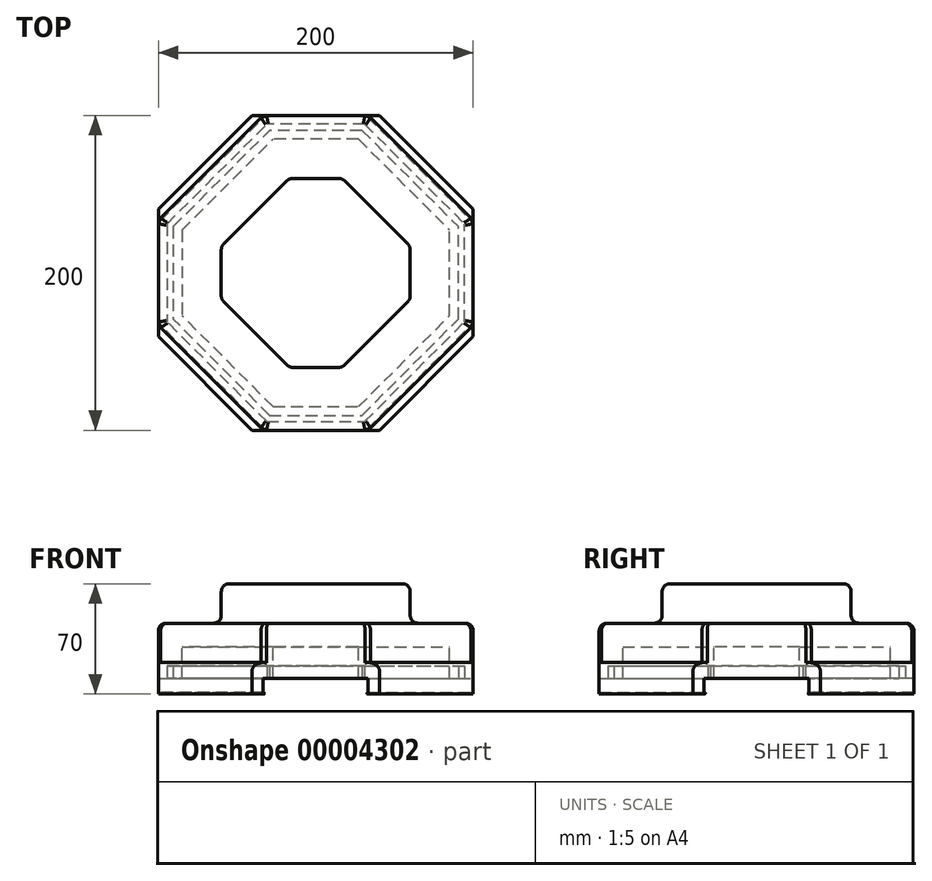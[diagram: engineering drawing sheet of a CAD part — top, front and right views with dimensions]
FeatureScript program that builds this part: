
annotation { "Feature Type Name" : "Feature", "Feature Type Description" : "" }
export const myFeature = defineFeature(function(context is Context, id is Id, definition is map)
    precondition{}
    {
        {
            var Q0;
            Q0=qCreatedBy(makeId("Top.planeOp"),FACE);
            var sketch = newSketch(context, id + "F0", { "sketchPlane" : qUnion([Q0])});
            skLineSegment(sketch, "E0", {"start": v(-113, -132.84) * mm, "end": v(87, -132.84) * mm});
            skLineSegment(sketch, "E1", {"start": v(87, -132.84) * mm, "end": v(87, 67.16) * mm});
            skLineSegment(sketch, "E2", {"start": v(87, 67.16) * mm, "end": v(-113, 67.16) * mm});
            skLineSegment(sketch, "E3", {"start": v(-113, 67.16) * mm, "end": v(-113, -132.84) * mm});
            skLineSegment(sketch, "E4.0", {"start": v(-113, -66.17) * mm, "end": v(87, -66.17) * mm});
            skLineSegment(sketch, "E5.0", {"start": v(-113, 0.5) * mm, "end": v(87, 0.5) * mm});
            skLineSegment(sketch, "E6.0", {"start": v(-46.33, 67.16) * mm, "end": v(-46.33, -132.84) * mm});
            skLineSegment(sketch, "E7.0", {"start": v(20.33, -132.84) * mm, "end": v(20.33, 67.16) * mm});
            skLineSegment(sketch, "E8", {"start": v(-46.33, -132.84) * mm, "end": v(-113, -66.17) * mm});
            skLineSegment(sketch, "E9", {"start": v(-113, 0.5) * mm, "end": v(-46.33, 67.16) * mm});
            skLineSegment(sketch, "E10", {"start": v(20.33, 67.16) * mm, "end": v(87, 0.5) * mm});
            skLineSegment(sketch, "E11", {"start": v(20.33, -132.84) * mm, "end": v(87, -66.17) * mm});
            skSolve(sketch);
        }
        {
            var Q0;
            {var subQ0=sQuery(id+"F0.wireOp",EDGE,"E8");Q0=makeQuery(id+"F0.imprint","IMPRINT",FACE,{"disambiguationData":[TD([[makeQuery(id+"F0.imprint","IMPRINT",EDGE,{"derivedFrom":subQ0}),-1.0]])]});}
            var Q1;
            {var subQ1=sQuery(id+"F0.wireOp",EDGE,"E4.0");var subQ5=sQuery(id+"F0.wireOp",EDGE,"E6.0");var subQ6=makeQuery(id+"F0.imprint","INTERSECT",VERTEX,{"derivedFrom":[subQ1,subQ5]});Q1=makeQuery(id+"F0.imprint","IMPRINT",FACE,{"disambiguationData":[TD([[makeQuery(id+"F0.imprint","IMPRINT",EDGE,{"disambiguationData":[TD([[subQ6,-1.0]])],"derivedFrom":subQ1}),-1.0]])]});}
            var Q2;
            {var subQ0=sQuery(id+"F0.wireOp",EDGE,"E11");Q2=makeQuery(id+"F0.imprint","IMPRINT",FACE,{"disambiguationData":[TD([[makeQuery(id+"F0.imprint","IMPRINT",EDGE,{"derivedFrom":subQ0}),1.0]])]});}
            var Q3;
            {var subQ0=sQuery(id+"F0.wireOp",EDGE,"E6.0");var subQ3=sQuery(id+"F0.wireOp",EDGE,"E4.0");var subQ4=makeQuery(id+"F0.imprint","INTERSECT",VERTEX,{"derivedFrom":[subQ3,subQ0]});Q3=makeQuery(id+"F0.imprint","IMPRINT",FACE,{"disambiguationData":[TD([[makeQuery(id+"F0.imprint","IMPRINT",EDGE,{"disambiguationData":[TD([[subQ4,1.0]])],"derivedFrom":subQ0}),-1.0]])]});}
            var Q4;
            {var subQ3=sQuery(id+"F0.wireOp",EDGE,"E4.0");var subQ5=sQuery(id+"F0.wireOp",EDGE,"E6.0");var subQ7=makeQuery(id+"F0.imprint","INTERSECT",VERTEX,{"derivedFrom":[subQ3,subQ5]});Q4=makeQuery(id+"F0.imprint","IMPRINT",FACE,{"disambiguationData":[TD([[makeQuery(id+"F0.imprint","IMPRINT",EDGE,{"disambiguationData":[TD([[subQ7,-1.0]])],"derivedFrom":subQ3}),1.0]])]});}
            var Q5;
            {var subQ0=sQuery(id+"F0.wireOp",EDGE,"E7.0");var subQ3=sQuery(id+"F0.wireOp",EDGE,"E4.0");var subQ4=makeQuery(id+"F0.imprint","INTERSECT",VERTEX,{"derivedFrom":[subQ3,subQ0]});Q5=makeQuery(id+"F0.imprint","IMPRINT",FACE,{"disambiguationData":[TD([[makeQuery(id+"F0.imprint","IMPRINT",EDGE,{"disambiguationData":[TD([[subQ4,-1.0]])],"derivedFrom":subQ0}),-1.0]])]});}
            var Q6;
            {var subQ0=sQuery(id+"F0.wireOp",EDGE,"E10");Q6=makeQuery(id+"F0.imprint","IMPRINT",FACE,{"disambiguationData":[TD([[makeQuery(id+"F0.imprint","IMPRINT",EDGE,{"derivedFrom":subQ0}),-1.0]])]});}
            var Q7;
            {var subQ1=sQuery(id+"F0.wireOp",EDGE,"E5.0");var subQ5=sQuery(id+"F0.wireOp",EDGE,"E6.0");var subQ6=makeQuery(id+"F0.imprint","INTERSECT",VERTEX,{"derivedFrom":[subQ1,subQ5]});Q7=makeQuery(id+"F0.imprint","IMPRINT",FACE,{"disambiguationData":[TD([[makeQuery(id+"F0.imprint","IMPRINT",EDGE,{"disambiguationData":[TD([[subQ6,-1.0]])],"derivedFrom":subQ1}),1.0]])]});}
            var Q8;
            {var subQ0=sQuery(id+"F0.wireOp",EDGE,"E9");Q8=makeQuery(id+"F0.imprint","IMPRINT",FACE,{"disambiguationData":[TD([[makeQuery(id+"F0.imprint","IMPRINT",EDGE,{"derivedFrom":subQ0}),-1.0]])]});}
            extrude(context, id + "F1", {"entities" : qUnion([Q0, Q1, Q2, Q3, Q4, Q5, Q6, Q7, Q8]), "oppositeDirection" : true, "depth" : 15 * mm});
        }
        {
            var Q0;
            Q0=makeQuery(id+"F1.opExtrude","CAP_FACE",FACE,{"disambiguationData":[OSD([sQuery(id+"F0.wireOp",EDGE,"E0"),sQuery(id+"F0.wireOp",EDGE,"E1"),sQuery(id+"F0.wireOp",EDGE,"E2"),sQuery(id+"F0.wireOp",EDGE,"E3"),sQuery(id+"F0.wireOp",EDGE,"E8"),sQuery(id+"F0.wireOp",EDGE,"E9"),sQuery(id+"F0.wireOp",EDGE,"E10"),sQuery(id+"F0.wireOp",EDGE,"E11")])],"isStart":true});
            var sketch = newSketch(context, id + "F2", { "sketchPlane" : qUnion([Q0])});
            skLineSegment(sketch, "E12.0", {"start": v(3.76, 27.16) * mm, "end": v(-29.76, 27.16) * mm});
            skLineSegment(sketch, "E12.1", {"start": v(-73, -16.07) * mm, "end": v(-29.76, 27.16) * mm});
            skLineSegment(sketch, "E12.2", {"start": v(-73, -16.07) * mm, "end": v(-73, -49.6) * mm});
            skLineSegment(sketch, "E12.3", {"start": v(-29.76, -92.84) * mm, "end": v(-73, -49.6) * mm});
            skLineSegment(sketch, "E12.4", {"start": v(-29.76, -92.84) * mm, "end": v(3.76, -92.84) * mm});
            skLineSegment(sketch, "E12.5", {"start": v(3.76, 27.16) * mm, "end": v(47, -16.07) * mm});
            skLineSegment(sketch, "E12.6", {"start": v(3.76, -92.84) * mm, "end": v(47, -49.6) * mm});
            skLineSegment(sketch, "E12.7", {"start": v(47, -49.6) * mm, "end": v(47, -16.07) * mm});
            skSolve(sketch);
        }
        {
            var Q0;
            Q0=makeQuery(id+"F2.imprint","IMPRINT",FACE,{"disambiguationData":[TD([[makeQuery(id+"F2.imprint","IMPRINT",EDGE,{"derivedFrom":sQuery(id+"F2.wireOp",EDGE,"E12.0")}),1.0]])]});
            extrude(context, id + "F3", {"entities" : qUnion([Q0]), "operationType" : NewBodyOperationType.ADD, "depth" : 25 * mm});
        }
        {
            var Q0;
            Q0=makeQuery(id+"F1.opExtrude","CAP_FACE",FACE,{"disambiguationData":[OSD([sQuery(id+"F0.wireOp",EDGE,"E0"),sQuery(id+"F0.wireOp",EDGE,"E1"),sQuery(id+"F0.wireOp",EDGE,"E2"),sQuery(id+"F0.wireOp",EDGE,"E3"),sQuery(id+"F0.wireOp",EDGE,"E8"),sQuery(id+"F0.wireOp",EDGE,"E9"),sQuery(id+"F0.wireOp",EDGE,"E10"),sQuery(id+"F0.wireOp",EDGE,"E11")])],"isStart":false});
            var sketch = newSketch(context, id + "F4", { "sketchPlane" : qUnion([Q0])});
            skLineSegment(sketch, "E13.0", {"start": v(-40.12, 117.84) * mm, "end": v(-98, 59.96) * mm});
            skLineSegment(sketch, "E13.1", {"start": v(-98, 5.72) * mm, "end": v(-98, 59.96) * mm});
            skLineSegment(sketch, "E13.2", {"start": v(-98, 5.72) * mm, "end": v(-40.12, -52.16) * mm});
            skLineSegment(sketch, "E13.3", {"start": v(14.12, -52.16) * mm, "end": v(-40.12, -52.16) * mm});
            skLineSegment(sketch, "E13.4", {"start": v(14.12, -52.16) * mm, "end": v(72, 5.72) * mm});
            skLineSegment(sketch, "E13.5", {"start": v(-40.12, 117.84) * mm, "end": v(14.12, 117.84) * mm});
            skLineSegment(sketch, "E13.6", {"start": v(72, 59.96) * mm, "end": v(72, 5.72) * mm});
            skLineSegment(sketch, "E13.7", {"start": v(14.12, 117.84) * mm, "end": v(72, 59.96) * mm});
            skSolve(sketch);
        }
        {
            var Q0;
            Q0=makeQuery(id+"F4.imprint","IMPRINT",FACE,{"disambiguationData":[TD([[makeQuery(id+"F4.imprint","IMPRINT",EDGE,{"derivedFrom":sQuery(id+"F4.wireOp",EDGE,"E13.0")}),-1.0]])]});
            extrude(context, id + "F5", {"entities" : qUnion([Q0]), "operationType" : NewBodyOperationType.ADD, "depth" : 20 * mm});
        }
        {
            var Q0;
            Q0=makeQuery(id+"F5.opExtrude","CAP_FACE",FACE,{"disambiguationData":[OSD([sQuery(id+"F0.wireOp",EDGE,"E0"),sQuery(id+"F0.wireOp",EDGE,"E1"),sQuery(id+"F0.wireOp",EDGE,"E2"),sQuery(id+"F0.wireOp",EDGE,"E3"),sQuery(id+"F0.wireOp",EDGE,"E8"),sQuery(id+"F0.wireOp",EDGE,"E9"),sQuery(id+"F0.wireOp",EDGE,"E10"),sQuery(id+"F0.wireOp",EDGE,"E11"),sQuery(id+"F4.wireOp",EDGE,"E13.0"),sQuery(id+"F4.wireOp",EDGE,"E13.1"),sQuery(id+"F4.wireOp",EDGE,"E13.2"),sQuery(id+"F4.wireOp",EDGE,"E13.3"),sQuery(id+"F4.wireOp",EDGE,"E13.4"),sQuery(id+"F4.wireOp",EDGE,"E13.5"),sQuery(id+"F4.wireOp",EDGE,"E13.6"),sQuery(id+"F4.wireOp",EDGE,"E13.7")])],"isStart":false});
            var sketch = newSketch(context, id + "F6", { "sketchPlane" : qUnion([Q0])});
            skLineSegment(sketch, "E14.0", {"start": v(-44.05, 127.34) * mm, "end": v(18.05, 127.34) * mm});
            skLineSegment(sketch, "E14.1", {"start": v(18.05, 127.34) * mm, "end": v(81.5, 63.9) * mm});
            skLineSegment(sketch, "E14.2", {"start": v(81.5, 63.9) * mm, "end": v(81.5, 1.78) * mm});
            skLineSegment(sketch, "E14.3", {"start": v(18.05, -61.66) * mm, "end": v(81.5, 1.78) * mm});
            skLineSegment(sketch, "E14.4", {"start": v(18.05, -61.66) * mm, "end": v(-44.05, -61.66) * mm});
            skLineSegment(sketch, "E14.5", {"start": v(-44.05, 127.34) * mm, "end": v(-107.5, 63.9) * mm});
            skLineSegment(sketch, "E14.6", {"start": v(-107.5, 1.78) * mm, "end": v(-44.05, -61.66) * mm});
            skLineSegment(sketch, "E14.7", {"start": v(-107.5, 1.78) * mm, "end": v(-107.5, 63.9) * mm});
            skLineSegment(sketch, "E15.0", {"start": v(-42.4, 123.34) * mm, "end": v(16.4, 123.34) * mm});
            skLineSegment(sketch, "E15.1", {"start": v(16.4, 123.34) * mm, "end": v(77.5, 62.24) * mm});
            skLineSegment(sketch, "E15.2", {"start": v(77.5, 62.24) * mm, "end": v(77.5, 3.44) * mm});
            skLineSegment(sketch, "E15.3", {"start": v(16.4, -57.66) * mm, "end": v(77.5, 3.44) * mm});
            skLineSegment(sketch, "E15.4", {"start": v(16.4, -57.66) * mm, "end": v(-42.4, -57.66) * mm});
            skLineSegment(sketch, "E15.5", {"start": v(-42.4, 123.34) * mm, "end": v(-103.5, 62.24) * mm});
            skLineSegment(sketch, "E15.6", {"start": v(-103.5, 3.44) * mm, "end": v(-42.4, -57.66) * mm});
            skLineSegment(sketch, "E15.7", {"start": v(-103.5, 3.44) * mm, "end": v(-103.5, 62.24) * mm});
            skSolve(sketch);
        }
        {
            var Q0;
            Q0=makeQuery(id+"F6.imprint","IMPRINT",FACE,{"disambiguationData":[TD([[makeQuery(id+"F6.imprint","IMPRINT",EDGE,{"derivedFrom":sQuery(id+"F6.wireOp",EDGE,"E14.0")}),-1.0]])]});
            extrude(context, id + "F7", {"entities" : qUnion([Q0]), "operationType" : NewBodyOperationType.REMOVE, "oppositeDirection" : true, "depth" : 8 * mm});
        }
        {
            var Q0;
            {var subQ0=sQuery(id+"F0.wireOp",EDGE,"E0");var subQ1=sQuery(id+"F0.wireOp",EDGE,"E1");var subQ2=sQuery(id+"F0.wireOp",EDGE,"E2");var subQ3=sQuery(id+"F0.wireOp",EDGE,"E3");var subQ4=sQuery(id+"F0.wireOp",EDGE,"E8");var subQ5=sQuery(id+"F0.wireOp",EDGE,"E9");var subQ6=sQuery(id+"F0.wireOp",EDGE,"E10");var subQ7=sQuery(id+"F0.wireOp",EDGE,"E11");Q0=makeQuery(id+"F7.boolean.opBoolean","SPLIT",FACE,{"disambiguationData":[TD([makeQuery(id+"F1.opExtrude","SWEPT_FACE",FACE,{"disambiguationData":[OSD([subQ0])]})])],"derivedFrom":makeQuery(id+"F5.opExtrude","CAP_FACE",FACE,{"disambiguationData":[OSD([subQ0,subQ1,subQ2,subQ3,subQ4,subQ5,subQ6,subQ7,sQuery(id+"F4.wireOp",EDGE,"E13.0"),sQuery(id+"F4.wireOp",EDGE,"E13.1"),sQuery(id+"F4.wireOp",EDGE,"E13.2"),sQuery(id+"F4.wireOp",EDGE,"E13.3"),sQuery(id+"F4.wireOp",EDGE,"E13.4"),sQuery(id+"F4.wireOp",EDGE,"E13.5"),sQuery(id+"F4.wireOp",EDGE,"E13.6"),sQuery(id+"F4.wireOp",EDGE,"E13.7")])],"isStart":false})});}
            var sketch = newSketch(context, id + "F8", { "sketchPlane" : qUnion([Q0])});
            skLineSegment(sketch, "E16.0", {"start": v(-49.87, 136.38) * mm, "end": v(-116.54, 69.7) * mm});
            skLineSegment(sketch, "E17", {"start": v(-116.54, 69.7) * mm, "end": v(-113, 66.17) * mm});
            skLineSegment(sketch, "E18", {"start": v(-113, 66.17) * mm, "end": v(-46.33, 132.84) * mm});
            skLineSegment(sketch, "E19", {"start": v(-46.33, 132.84) * mm, "end": v(-49.87, 136.38) * mm});
            skLineSegment(sketch, "E20.0", {"start": v(23.87, 136.38) * mm, "end": v(90.54, 69.7) * mm});
            skLineSegment(sketch, "E21.0", {"start": v(23.86, -70.7) * mm, "end": v(90.53, -4.03) * mm});
            skLineSegment(sketch, "E22.0", {"start": v(-116.54, -4.03) * mm, "end": v(-49.87, -70.7) * mm});
            skLineSegment(sketch, "E23", {"start": v(-116.54, -4.03) * mm, "end": v(-113, -0.5) * mm});
            skLineSegment(sketch, "E24", {"start": v(-113, -0.5) * mm, "end": v(-46.33, -67.16) * mm});
            skLineSegment(sketch, "E25", {"start": v(-46.33, -67.16) * mm, "end": v(-49.87, -70.7) * mm});
            skLineSegment(sketch, "E26", {"start": v(20.33, -67.16) * mm, "end": v(23.86, -70.7) * mm});
            skLineSegment(sketch, "E27", {"start": v(90.53, -4.03) * mm, "end": v(87, -0.5) * mm});
            skLineSegment(sketch, "E28", {"start": v(87, -0.5) * mm, "end": v(20.33, -67.16) * mm});
            skLineSegment(sketch, "E29", {"start": v(90.54, 69.7) * mm, "end": v(87, 66.17) * mm});
            skLineSegment(sketch, "E30", {"start": v(87, 66.17) * mm, "end": v(20.33, 132.84) * mm});
            skLineSegment(sketch, "E31", {"start": v(20.33, 132.84) * mm, "end": v(23.87, 136.38) * mm});
            skSolve(sketch);
        }
        {
            var Q0;
            Q0=makeQuery(id+"F8.imprint","IMPRINT",FACE,{"disambiguationData":[TD([[makeQuery(id+"F8.imprint","IMPRINT",EDGE,{"derivedFrom":sQuery(id+"F8.wireOp",EDGE,"E22.0")}),1.0]])]});
            var Q1;
            Q1=makeQuery(id+"F8.imprint","IMPRINT",FACE,{"disambiguationData":[TD([[makeQuery(id+"F8.imprint","IMPRINT",EDGE,{"derivedFrom":sQuery(id+"F8.wireOp",EDGE,"E16.0")}),1.0]])]});
            var Q2;
            Q2=makeQuery(id+"F8.imprint","IMPRINT",FACE,{"disambiguationData":[TD([[makeQuery(id+"F8.imprint","IMPRINT",EDGE,{"derivedFrom":sQuery(id+"F8.wireOp",EDGE,"E20.0")}),-1.0]])]});
            var Q3;
            Q3=makeQuery(id+"F8.imprint","IMPRINT",FACE,{"disambiguationData":[TD([[makeQuery(id+"F8.imprint","IMPRINT",EDGE,{"derivedFrom":sQuery(id+"F8.wireOp",EDGE,"E21.0")}),1.0]])]});
            extrude(context, id + "F9", {"entities" : qUnion([Q0, Q1, Q2, Q3]), "operationType" : NewBodyOperationType.ADD, "endBound" : BoundingType.SYMMETRIC, "depth" : 20 * mm});
        }
        {
            var Q0;
            Q0=makeQuery(id+"F9.opExtrude","CAP_FACE",FACE,{"disambiguationData":[OSD([sQuery(id+"F8.wireOp",EDGE,"E22.0"),sQuery(id+"F8.wireOp",EDGE,"E23"),sQuery(id+"F8.wireOp",EDGE,"E24"),sQuery(id+"F8.wireOp",EDGE,"E25")])],"isStart":false});
            var sketch = newSketch(context, id + "F10", { "sketchPlane" : qUnion([Q0])});
            skLineSegment(sketch, "E32", {"start": v(-113, -0.5) * mm, "end": v(-113, -7.57) * mm});
            skLineSegment(sketch, "E33", {"start": v(-46.33, -67.16) * mm, "end": v(-53.4, -67.16) * mm});
            skSolve(sketch);
        }
        {
            var Q0;
            Q0=makeQuery(id+"F9.opExtrude","CAP_FACE",FACE,{"disambiguationData":[OSD([sQuery(id+"F8.wireOp",EDGE,"E21.0"),sQuery(id+"F8.wireOp",EDGE,"E26"),sQuery(id+"F8.wireOp",EDGE,"E27"),sQuery(id+"F8.wireOp",EDGE,"E28")])],"isStart":false});
            var sketch = newSketch(context, id + "F11", { "sketchPlane" : qUnion([Q0])});
            skLineSegment(sketch, "E34", {"start": v(20.33, -67.16) * mm, "end": v(27.4, -67.16) * mm});
            skLineSegment(sketch, "E35", {"start": v(87, -0.5) * mm, "end": v(87, -7.57) * mm});
            skSolve(sketch);
        }
        {
            var Q0;
            Q0=makeQuery(id+"F9.opExtrude","CAP_FACE",FACE,{"disambiguationData":[OSD([sQuery(id+"F8.wireOp",EDGE,"E20.0"),sQuery(id+"F8.wireOp",EDGE,"E29"),sQuery(id+"F8.wireOp",EDGE,"E30"),sQuery(id+"F8.wireOp",EDGE,"E31")])],"isStart":false});
            var sketch = newSketch(context, id + "F12", { "sketchPlane" : qUnion([Q0])});
            skLineSegment(sketch, "E36", {"start": v(87, 66.17) * mm, "end": v(87, 73.24) * mm});
            skLineSegment(sketch, "E37", {"start": v(20.33, 132.84) * mm, "end": v(27.4, 132.84) * mm});
            skSolve(sketch);
        }
        {
            var Q0;
            Q0=makeQuery(id+"F9.opExtrude","CAP_FACE",FACE,{"disambiguationData":[OSD([sQuery(id+"F8.wireOp",EDGE,"E16.0"),sQuery(id+"F8.wireOp",EDGE,"E17"),sQuery(id+"F8.wireOp",EDGE,"E18"),sQuery(id+"F8.wireOp",EDGE,"E19")])],"isStart":false});
            var sketch = newSketch(context, id + "F13", { "sketchPlane" : qUnion([Q0])});
            skLineSegment(sketch, "E38", {"start": v(-113, 66.17) * mm, "end": v(-113, 73.24) * mm});
            skLineSegment(sketch, "E39", {"start": v(-46.33, 132.84) * mm, "end": v(-53.4, 132.84) * mm});
            skSolve(sketch);
        }
        {
            var Q0;
            {var subQ1=sQuery(id+"F10.wireOp",EDGE,"E32");Q0=makeQuery(id+"F10.imprint","IMPRINT",FACE,{"disambiguationData":[TD([[makeQuery(id+"F10.imprint","IMPRINT",EDGE,{"derivedFrom":subQ1}),-1.0]])]});}
            var Q1;
            {var subQ1=sQuery(id+"F10.wireOp",EDGE,"E33");Q1=makeQuery(id+"F10.imprint","IMPRINT",FACE,{"disambiguationData":[TD([[makeQuery(id+"F10.imprint","IMPRINT",EDGE,{"derivedFrom":subQ1}),1.0]])]});}
            var Q2;
            {var subQ1=sQuery(id+"F11.wireOp",EDGE,"E34");Q2=makeQuery(id+"F11.imprint","IMPRINT",FACE,{"disambiguationData":[TD([[makeQuery(id+"F11.imprint","IMPRINT",EDGE,{"derivedFrom":subQ1}),-1.0]])]});}
            var Q3;
            {var subQ1=sQuery(id+"F11.wireOp",EDGE,"E35");Q3=makeQuery(id+"F11.imprint","IMPRINT",FACE,{"disambiguationData":[TD([[makeQuery(id+"F11.imprint","IMPRINT",EDGE,{"derivedFrom":subQ1}),1.0]])]});}
            var Q4;
            {var subQ1=sQuery(id+"F12.wireOp",EDGE,"E36");Q4=makeQuery(id+"F12.imprint","IMPRINT",FACE,{"disambiguationData":[TD([[makeQuery(id+"F12.imprint","IMPRINT",EDGE,{"derivedFrom":subQ1}),-1.0]])]});}
            var Q5;
            {var subQ1=sQuery(id+"F12.wireOp",EDGE,"E37");Q5=makeQuery(id+"F12.imprint","IMPRINT",FACE,{"disambiguationData":[TD([[makeQuery(id+"F12.imprint","IMPRINT",EDGE,{"derivedFrom":subQ1}),1.0]])]});}
            var Q6;
            {var subQ1=sQuery(id+"F13.wireOp",EDGE,"E39");Q6=makeQuery(id+"F13.imprint","IMPRINT",FACE,{"disambiguationData":[TD([[makeQuery(id+"F13.imprint","IMPRINT",EDGE,{"derivedFrom":subQ1}),-1.0]])]});}
            var Q7;
            {var subQ1=sQuery(id+"F13.wireOp",EDGE,"E38");Q7=makeQuery(id+"F13.imprint","IMPRINT",FACE,{"disambiguationData":[TD([[makeQuery(id+"F13.imprint","IMPRINT",EDGE,{"derivedFrom":subQ1}),1.0]])]});}
            extrude(context, id + "F14", {"entities" : qUnion([Q0, Q1, Q2, Q3, Q4, Q5, Q6, Q7]), "operationType" : NewBodyOperationType.REMOVE, "oppositeDirection" : true, "depth" : 25 * mm});
        }
        {
            var Q0;
            Q0=makeQuery(id+"F9.opExtrude","SWEPT_FACE",FACE,{"disambiguationData":[OSD([sQuery(id+"F8.wireOp",EDGE,"E18")])]});
            var sketch = newSketch(context, id + "F15", { "sketchPlane" : qUnion([Q0])});
            skLineSegment(sketch, "E40.0", {"start": v(-61.17, -44) * mm, "end": v(33.11, -44) * mm});
            skSolve(sketch);
        }
        {
            var Q0;
            {var subQ3=sQuery(id+"F15.wireOp",EDGE,"E40.0");Q0=makeQuery(id+"F15.imprint","IMPRINT",FACE,{"disambiguationData":[TD([[makeQuery(id+"F15.imprint","IMPRINT",EDGE,{"derivedFrom":subQ3}),-1.0]])]});}
            extrude(context, id + "F16", {"entities" : qUnion([Q0]), "operationType" : NewBodyOperationType.ADD, "depth" : 1 * mm});
        }
        {
            var Q0;
            Q0=makeQuery(id+"F9.opExtrude","SWEPT_FACE",FACE,{"disambiguationData":[OSD([sQuery(id+"F8.wireOp",EDGE,"E24")])]});
            var sketch = newSketch(context, id + "F17", { "sketchPlane" : qUnion([Q0])});
            skLineSegment(sketch, "E41.0", {"start": v(-79.56, -44) * mm, "end": v(14.72, -44) * mm});
            skSolve(sketch);
        }
        {
            var Q0;
            {var subQ3=sQuery(id+"F17.wireOp",EDGE,"E41.0");Q0=makeQuery(id+"F17.imprint","IMPRINT",FACE,{"disambiguationData":[TD([[makeQuery(id+"F17.imprint","IMPRINT",EDGE,{"derivedFrom":subQ3}),-1.0]])]});}
            extrude(context, id + "F18", {"entities" : qUnion([Q0]), "operationType" : NewBodyOperationType.ADD, "depth" : 1 * mm});
        }
        {
            var Q0;
            Q0=makeQuery(id+"F9.opExtrude","SWEPT_FACE",FACE,{"disambiguationData":[OSD([sQuery(id+"F8.wireOp",EDGE,"E28")])]});
            var sketch = newSketch(context, id + "F19", { "sketchPlane" : qUnion([Q0])});
            skLineSegment(sketch, "E42.0", {"start": v(-33.1, -44) * mm, "end": v(61.17, -44) * mm});
            skLineSegment(sketch, "E43", {"start": v(61.17, -35) * mm, "end": v(61.17, -45) * mm});
            skSolve(sketch);
        }
        {
            var Q0;
            {var subQ3=sQuery(id+"F19.wireOp",EDGE,"E42.0");Q0=makeQuery(id+"F19.imprint","IMPRINT",FACE,{"disambiguationData":[TD([[makeQuery(id+"F19.imprint","IMPRINT",EDGE,{"derivedFrom":subQ3}),-1.0]])]});}
            extrude(context, id + "F20", {"entities" : qUnion([Q0]), "operationType" : NewBodyOperationType.ADD, "depth" : 1 * mm});
        }
        {
            var Q0;
            Q0=makeQuery(id+"F9.opExtrude","SWEPT_FACE",FACE,{"disambiguationData":[OSD([sQuery(id+"F8.wireOp",EDGE,"E30")])]});
            var sketch = newSketch(context, id + "F21", { "sketchPlane" : qUnion([Q0])});
            skLineSegment(sketch, "E44.0", {"start": v(79.56, -44) * mm, "end": v(-14.73, -44) * mm});
            skSolve(sketch);
        }
        {
            var Q0;
            {var subQ3=sQuery(id+"F21.wireOp",EDGE,"E44.0");Q0=makeQuery(id+"F21.imprint","IMPRINT",FACE,{"disambiguationData":[TD([[makeQuery(id+"F21.imprint","IMPRINT",EDGE,{"derivedFrom":subQ3}),1.0]])]});}
            extrude(context, id + "F22", {"entities" : qUnion([Q0]), "operationType" : NewBodyOperationType.ADD, "depth" : 1 * mm});
        }
        {
            var Q0;
            Q0=makeQuery(id+"F22.opExtrude","CAP_EDGE",EDGE,{"disambiguationData":[OSD([sQuery(id+"F8.wireOp",EDGE,"E30")])],"isStart":false});
            var Q1;
            Q1=makeQuery(id+"F22.opExtrude","CAP_EDGE",EDGE,{"disambiguationData":[OSD([sQuery(id+"F21.wireOp",EDGE,"E44.0")])],"isStart":false});
            var Q2;
            Q2=makeQuery(id+"F16.opExtrude","CAP_FACE",FACE,{"disambiguationData":[OSD([sQuery(id+"F0.wireOp",EDGE,"E0"),sQuery(id+"F0.wireOp",EDGE,"E3"),sQuery(id+"F8.wireOp",EDGE,"E17"),sQuery(id+"F8.wireOp",EDGE,"E18"),sQuery(id+"F8.wireOp",EDGE,"E19"),sQuery(id+"F13.wireOp",EDGE,"E38"),sQuery(id+"F13.wireOp",EDGE,"E39"),sQuery(id+"F15.wireOp",EDGE,"E40.0")])],"isStart":false});
            var Q3;
            Q3=makeQuery(id+"F18.opExtrude","CAP_FACE",FACE,{"disambiguationData":[OSD([sQuery(id+"F0.wireOp",EDGE,"E2"),sQuery(id+"F0.wireOp",EDGE,"E3"),sQuery(id+"F8.wireOp",EDGE,"E23"),sQuery(id+"F8.wireOp",EDGE,"E24"),sQuery(id+"F8.wireOp",EDGE,"E25"),sQuery(id+"F10.wireOp",EDGE,"E32"),sQuery(id+"F10.wireOp",EDGE,"E33"),sQuery(id+"F17.wireOp",EDGE,"E41.0")])],"isStart":false});
            var Q4;
            Q4=makeQuery(id+"F20.opExtrude","CAP_FACE",FACE,{"disambiguationData":[OSD([sQuery(id+"F0.wireOp",EDGE,"E2"),sQuery(id+"F8.wireOp",EDGE,"E26"),sQuery(id+"F8.wireOp",EDGE,"E28"),sQuery(id+"F11.wireOp",EDGE,"E34"),sQuery(id+"F19.wireOp",EDGE,"E42.0"),sQuery(id+"F19.wireOp",EDGE,"E43")])],"isStart":false});
            fillet(context, id + "F23", {"entities" : qUnion([Q0, Q1, Q2, Q3, Q4]), "radius" : 0.5 * mm, "tangentPropagation" : true, "allowEdgeOverflow" : false});
        }
        {
            var Q0;
            Q0=makeQuery(id+"F9.opExtrude","CAP_EDGE",EDGE,{"disambiguationData":[OSD([sQuery(id+"F8.wireOp",EDGE,"E22.0")])],"isStart":true});
            var Q1;
            Q1=makeQuery(id+"F9.opExtrude","CAP_EDGE",EDGE,{"disambiguationData":[OSD([sQuery(id+"F8.wireOp",EDGE,"E16.0")])],"isStart":true});
            var Q2;
            Q2=makeQuery(id+"F9.opExtrude","CAP_EDGE",EDGE,{"disambiguationData":[OSD([sQuery(id+"F8.wireOp",EDGE,"E20.0")])],"isStart":true});
            var Q3;
            Q3=makeQuery(id+"F9.opExtrude","CAP_EDGE",EDGE,{"disambiguationData":[OSD([sQuery(id+"F8.wireOp",EDGE,"E21.0")])],"isStart":true});
            fillet(context, id + "F24", {"entities" : qUnion([Q0, Q1, Q2, Q3]), "radius" : 5 * mm, "tangentPropagation" : true, "allowEdgeOverflow" : false});
        }
        {
            var Q0;
            {var subQ0=sQuery(id+"F0.wireOp",EDGE,"E8");var subQ1=sQuery(id+"F0.wireOp",EDGE,"E3");Q0=makeQuery(id+"F9.boolean.opBoolean","SPLIT",EDGE,{"derivedFrom":makeQuery(id+"F5.boolean.opBoolean","MERGE",EDGE,{"derivedFrom":[makeQuery(id+"F1.opExtrude","SWEPT_EDGE",EDGE,{"disambiguationData":[OSD([subQ1,sQuery(id+"F0.wireOp",EDGE,"E4.0"),subQ0])]}),makeQuery(id+"F5.opExtrude","SWEPT_EDGE",EDGE,{"disambiguationData":[OSD([subQ1,subQ0])]})]})});}
            var Q1;
            {var subQ0=sQuery(id+"F0.wireOp",EDGE,"E9");var subQ1=sQuery(id+"F0.wireOp",EDGE,"E3");Q1=makeQuery(id+"F9.boolean.opBoolean","SPLIT",EDGE,{"derivedFrom":makeQuery(id+"F5.boolean.opBoolean","MERGE",EDGE,{"derivedFrom":[makeQuery(id+"F1.opExtrude","SWEPT_EDGE",EDGE,{"disambiguationData":[OSD([subQ1,sQuery(id+"F0.wireOp",EDGE,"E5.0"),subQ0])]}),makeQuery(id+"F5.opExtrude","SWEPT_EDGE",EDGE,{"disambiguationData":[OSD([subQ1,subQ0])]})]})});}
            var Q2;
            {var subQ0=sQuery(id+"F0.wireOp",EDGE,"E9");var subQ1=sQuery(id+"F0.wireOp",EDGE,"E2");Q2=makeQuery(id+"F9.boolean.opBoolean","SPLIT",EDGE,{"derivedFrom":makeQuery(id+"F5.boolean.opBoolean","MERGE",EDGE,{"derivedFrom":[makeQuery(id+"F1.opExtrude","SWEPT_EDGE",EDGE,{"disambiguationData":[OSD([subQ1,sQuery(id+"F0.wireOp",EDGE,"E6.0"),subQ0])]}),makeQuery(id+"F5.opExtrude","SWEPT_EDGE",EDGE,{"disambiguationData":[OSD([subQ1,subQ0])]})]})});}
            var Q3;
            {var subQ0=sQuery(id+"F0.wireOp",EDGE,"E10");var subQ1=sQuery(id+"F0.wireOp",EDGE,"E2");Q3=makeQuery(id+"F9.boolean.opBoolean","SPLIT",EDGE,{"derivedFrom":makeQuery(id+"F5.boolean.opBoolean","MERGE",EDGE,{"derivedFrom":[makeQuery(id+"F1.opExtrude","SWEPT_EDGE",EDGE,{"disambiguationData":[OSD([subQ1,sQuery(id+"F0.wireOp",EDGE,"E7.0"),subQ0])]}),makeQuery(id+"F5.opExtrude","SWEPT_EDGE",EDGE,{"disambiguationData":[OSD([subQ1,subQ0])]})]})});}
            var Q4;
            {var subQ0=sQuery(id+"F0.wireOp",EDGE,"E10");var subQ1=sQuery(id+"F0.wireOp",EDGE,"E1");Q4=makeQuery(id+"F9.boolean.opBoolean","SPLIT",EDGE,{"derivedFrom":makeQuery(id+"F5.boolean.opBoolean","MERGE",EDGE,{"derivedFrom":[makeQuery(id+"F1.opExtrude","SWEPT_EDGE",EDGE,{"disambiguationData":[OSD([subQ1,sQuery(id+"F0.wireOp",EDGE,"E5.0"),subQ0])]}),makeQuery(id+"F5.opExtrude","SWEPT_EDGE",EDGE,{"disambiguationData":[OSD([subQ1,subQ0])]})]})});}
            var Q5;
            {var subQ0=sQuery(id+"F0.wireOp",EDGE,"E11");var subQ1=sQuery(id+"F0.wireOp",EDGE,"E1");Q5=makeQuery(id+"F9.boolean.opBoolean","SPLIT",EDGE,{"derivedFrom":makeQuery(id+"F5.boolean.opBoolean","MERGE",EDGE,{"derivedFrom":[makeQuery(id+"F1.opExtrude","SWEPT_EDGE",EDGE,{"disambiguationData":[OSD([subQ1,sQuery(id+"F0.wireOp",EDGE,"E4.0"),subQ0])]}),makeQuery(id+"F5.opExtrude","SWEPT_EDGE",EDGE,{"disambiguationData":[OSD([subQ1,subQ0])]})]})});}
            var Q6;
            {var subQ0=sQuery(id+"F0.wireOp",EDGE,"E11");var subQ1=sQuery(id+"F0.wireOp",EDGE,"E0");Q6=makeQuery(id+"F9.boolean.opBoolean","SPLIT",EDGE,{"derivedFrom":makeQuery(id+"F5.boolean.opBoolean","MERGE",EDGE,{"derivedFrom":[makeQuery(id+"F1.opExtrude","SWEPT_EDGE",EDGE,{"disambiguationData":[OSD([subQ1,sQuery(id+"F0.wireOp",EDGE,"E7.0"),subQ0])]}),makeQuery(id+"F5.opExtrude","SWEPT_EDGE",EDGE,{"disambiguationData":[OSD([subQ1,subQ0])]})]})});}
            var Q7;
            {var subQ0=sQuery(id+"F0.wireOp",EDGE,"E8");var subQ1=sQuery(id+"F0.wireOp",EDGE,"E0");Q7=makeQuery(id+"F9.boolean.opBoolean","SPLIT",EDGE,{"derivedFrom":makeQuery(id+"F5.boolean.opBoolean","MERGE",EDGE,{"derivedFrom":[makeQuery(id+"F1.opExtrude","SWEPT_EDGE",EDGE,{"disambiguationData":[OSD([subQ1,sQuery(id+"F0.wireOp",EDGE,"E6.0"),subQ0])]}),makeQuery(id+"F5.opExtrude","SWEPT_EDGE",EDGE,{"disambiguationData":[OSD([subQ1,subQ0])]})]})});}
            chamfer(context, id + "F25", {"entities" : qUnion([Q0, Q1, Q2, Q3, Q4, Q5, Q6, Q7]), "width" : 5 * mm});
        }
        {
            var Q0;
            Q0=makeQuery(id+"F3.opExtrude","CAP_FACE",FACE,{"disambiguationData":[OSD([sQuery(id+"F2.wireOp",EDGE,"E12.0"),sQuery(id+"F2.wireOp",EDGE,"E12.1"),sQuery(id+"F2.wireOp",EDGE,"E12.2"),sQuery(id+"F2.wireOp",EDGE,"E12.3"),sQuery(id+"F2.wireOp",EDGE,"E12.4"),sQuery(id+"F2.wireOp",EDGE,"E12.5"),sQuery(id+"F2.wireOp",EDGE,"E12.6"),sQuery(id+"F2.wireOp",EDGE,"E12.7")])],"isStart":false});
            var Q1;
            Q1=makeQuery(id+"F1.opExtrude","CAP_FACE",FACE,{"disambiguationData":[OSD([sQuery(id+"F0.wireOp",EDGE,"E0"),sQuery(id+"F0.wireOp",EDGE,"E1"),sQuery(id+"F0.wireOp",EDGE,"E2"),sQuery(id+"F0.wireOp",EDGE,"E3"),sQuery(id+"F0.wireOp",EDGE,"E8"),sQuery(id+"F0.wireOp",EDGE,"E9"),sQuery(id+"F0.wireOp",EDGE,"E10"),sQuery(id+"F0.wireOp",EDGE,"E11")])],"isStart":true});
            var Q2;
            Q2=makeQuery(id+"F3.opExtrude","SWEPT_FACE",FACE,{"disambiguationData":[OSD([sQuery(id+"F2.wireOp",EDGE,"E12.1")])]});
            var Q3;
            Q3=makeQuery(id+"F3.opExtrude","SWEPT_FACE",FACE,{"disambiguationData":[OSD([sQuery(id+"F2.wireOp",EDGE,"E12.2")])]});
            var Q4;
            Q4=makeQuery(id+"F3.opExtrude","SWEPT_FACE",FACE,{"disambiguationData":[OSD([sQuery(id+"F2.wireOp",EDGE,"E12.3")])]});
            var Q5;
            Q5=makeQuery(id+"F3.opExtrude","SWEPT_FACE",FACE,{"disambiguationData":[OSD([sQuery(id+"F2.wireOp",EDGE,"E12.4")])]});
            var Q6;
            Q6=makeQuery(id+"F3.opExtrude","SWEPT_FACE",FACE,{"disambiguationData":[OSD([sQuery(id+"F2.wireOp",EDGE,"E12.6")])]});
            var Q7;
            Q7=makeQuery(id+"F3.opExtrude","SWEPT_FACE",FACE,{"disambiguationData":[OSD([sQuery(id+"F2.wireOp",EDGE,"E12.7")])]});
            var Q8;
            Q8=makeQuery(id+"F3.opExtrude","SWEPT_FACE",FACE,{"disambiguationData":[OSD([sQuery(id+"F2.wireOp",EDGE,"E12.5")])]});
            var Q9;
            Q9=makeQuery(id+"F3.opExtrude","SWEPT_FACE",FACE,{"disambiguationData":[OSD([sQuery(id+"F2.wireOp",EDGE,"E12.0")])]});
            fillet(context, id + "F26", {"entities" : qUnion([Q0, Q1, Q2, Q3, Q4, Q5, Q6, Q7, Q8, Q9]), "radius" : 5 * mm, "tangentPropagation" : true, "allowEdgeOverflow" : false});
        }
    });
